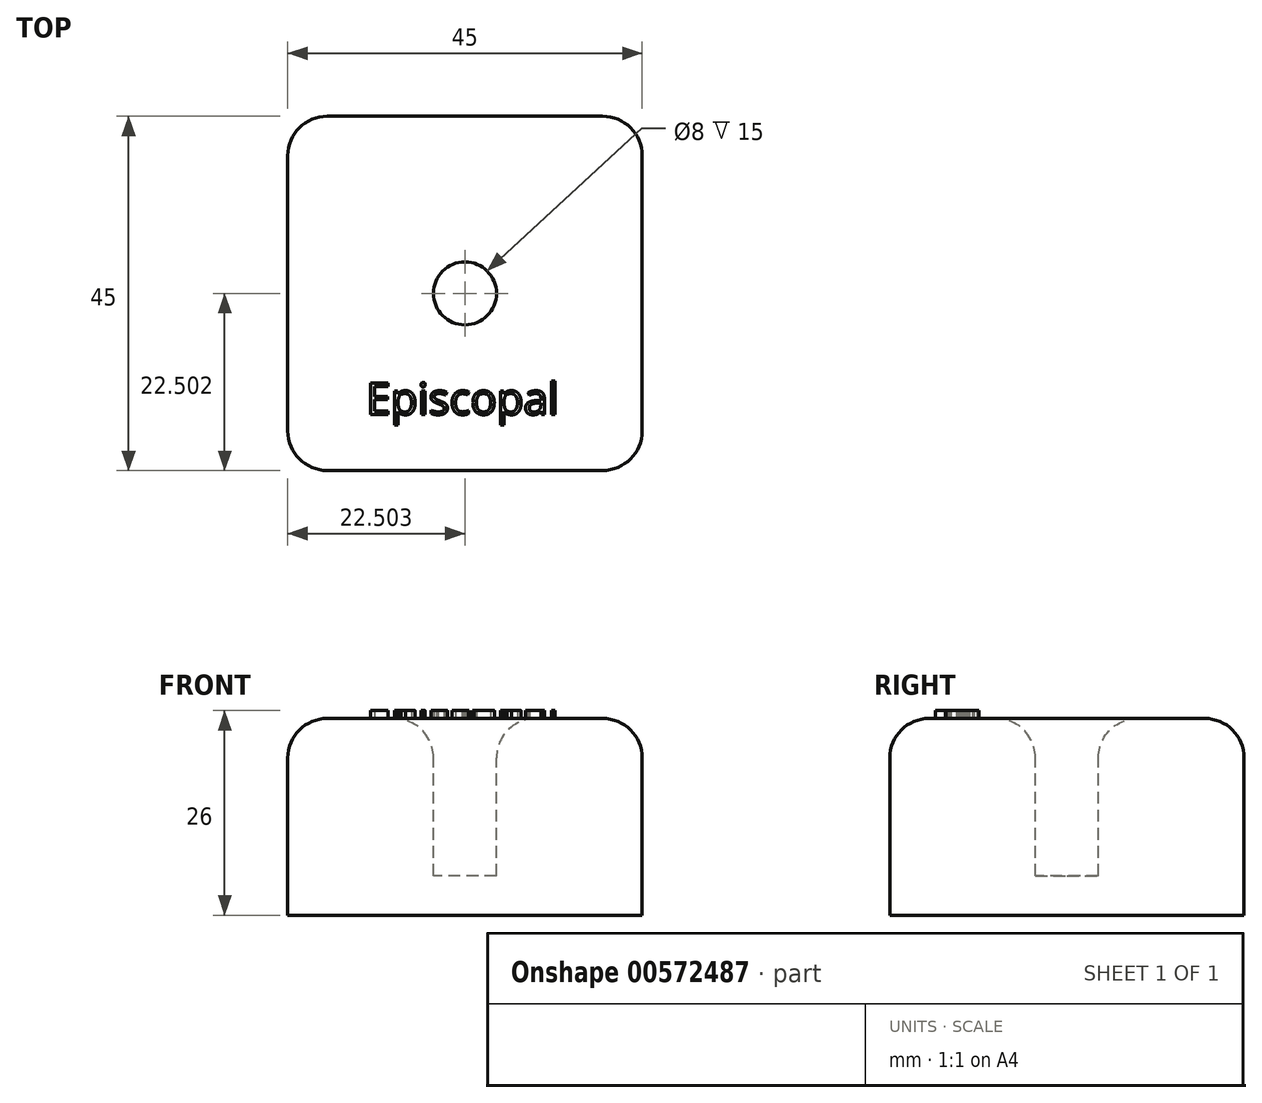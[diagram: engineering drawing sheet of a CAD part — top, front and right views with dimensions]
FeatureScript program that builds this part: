
annotation { "Feature Type Name" : "Feature", "Feature Type Description" : "" }
export const myFeature = defineFeature(function(context is Context, id is Id, definition is map)
    precondition{}
    {
        {
            var Q0;
            Q0=qCreatedBy(makeId("Top.planeOp"),FACE);
            var sketch = newSketch(context, id + "F0", { "sketchPlane" : qUnion([Q0])});
            skLineSegment(sketch, "E0.bottom", {"start": v(-22.96, 30.91) * mm, "end": v(22.04, 30.91) * mm});
            skLineSegment(sketch, "E0.top", {"start": v(-22.96, -14.09) * mm, "end": v(22.04, -14.09) * mm});
            skLineSegment(sketch, "E0.left", {"start": v(-22.96, 30.91) * mm, "end": v(-22.96, -14.09) * mm});
            skLineSegment(sketch, "E0.right", {"start": v(22.04, 30.91) * mm, "end": v(22.04, -14.09) * mm});
            skSolve(sketch);
        }
        {
            var Q0;
            Q0=makeQuery(id+"F0.imprint","IMPRINT",FACE,{"disambiguationData":[TD([[makeQuery(id+"F0.imprint","IMPRINT",EDGE,{"derivedFrom":sQuery(id+"F0.wireOp",EDGE,"E0.bottom")}),-1.0]])]});
            extrude(context, id + "F1", {"entities" : qUnion([Q0]), "depth" : 25 * mm, "offsetDistance" : 25 * mm});
        }
        {
            var Q0;
            Q0=makeQuery(id+"F1.opExtrude","CAP_FACE",FACE,{"disambiguationData":[OSD([sQuery(id+"F0.wireOp",EDGE,"E0.bottom"),sQuery(id+"F0.wireOp",EDGE,"E0.top"),sQuery(id+"F0.wireOp",EDGE,"E0.left"),sQuery(id+"F0.wireOp",EDGE,"E0.right")])],"isStart":false});
            var sketch = newSketch(context, id + "F2", { "sketchPlane" : qUnion([Q0])});
            skCircle(sketch, "E1", {"center": v(-0.46, 8.41) * mm, "radius": 4 * mm});
            skSolve(sketch);
        }
        {
            var Q0;
            Q0=makeQuery(id+"F2.imprint","IMPRINT",FACE,{"disambiguationData":[TD([[makeQuery(id+"F2.imprint","IMPRINT",EDGE,{"derivedFrom":sQuery(id+"F2.wireOp",EDGE,"E1")}),1.0]])]});
            extrude(context, id + "F3", {"entities" : qUnion([Q0]), "operationType" : NewBodyOperationType.REMOVE, "oppositeDirection" : true, "depth" : 20 * mm, "offsetDistance" : 25 * mm});
        }
        {
            var Q0;
            Q0=makeQuery(id+"F1.opExtrude","CAP_FACE",FACE,{"disambiguationData":[OSD([sQuery(id+"F0.wireOp",EDGE,"E0.bottom"),sQuery(id+"F0.wireOp",EDGE,"E0.top"),sQuery(id+"F0.wireOp",EDGE,"E0.left"),sQuery(id+"F0.wireOp",EDGE,"E0.right")])],"isStart":false});
            var Q1;
            Q1=makeQuery(id+"F1.opExtrude","SWEPT_EDGE",EDGE,{"disambiguationData":[OSD([sQuery(id+"F0.wireOp",EDGE,"E0.bottom"),sQuery(id+"F0.wireOp",EDGE,"E0.left")])]});
            var Q2;
            Q2=makeQuery(id+"F1.opExtrude","SWEPT_EDGE",EDGE,{"disambiguationData":[OSD([sQuery(id+"F0.wireOp",EDGE,"E0.bottom"),sQuery(id+"F0.wireOp",EDGE,"E0.right")])]});
            var Q3;
            Q3=makeQuery(id+"F1.opExtrude","SWEPT_EDGE",EDGE,{"disambiguationData":[OSD([sQuery(id+"F0.wireOp",EDGE,"E0.top"),sQuery(id+"F0.wireOp",EDGE,"E0.right")])]});
            var Q4;
            Q4=makeQuery(id+"F1.opExtrude","SWEPT_EDGE",EDGE,{"disambiguationData":[OSD([sQuery(id+"F0.wireOp",EDGE,"E0.top"),sQuery(id+"F0.wireOp",EDGE,"E0.left")])]});
            fillet(context, id + "F4", {"entities" : qUnion([Q0, Q1, Q2, Q3, Q4]), "radius" : 5 * mm, "tangentPropagation" : true, "allowEdgeOverflow" : false});
        }
        {
            var Q0;
            Q0=makeQuery(id+"F1.opExtrude","CAP_FACE",FACE,{"disambiguationData":[OSD([sQuery(id+"F0.wireOp",EDGE,"E0.bottom"),sQuery(id+"F0.wireOp",EDGE,"E0.top"),sQuery(id+"F0.wireOp",EDGE,"E0.left"),sQuery(id+"F0.wireOp",EDGE,"E0.right")])],"isStart":false});
            var sketch = newSketch(context, id + "F5", { "sketchPlane" : qUnion([Q0])});
            skText(sketch, "E2", { "text": "Episcopal", "fontName": "OpenSans-Regular.ttf"});
            const initialGuessF5  = {"E2": [-0.01297, -0.00697, 1, 0, 0.004]};
            skSetInitialGuess(sketch, initialGuessF5);
            skSolve(sketch);
        }
        {
            var Q0;
            Q0 = qSketchRegion(id + "F5", true);
            extrude(context, id + "F6", {"entities" : qUnion([Q0]), "operationType" : NewBodyOperationType.ADD, "depth" : 1 * mm, "offsetDistance" : 25 * mm});
        }
    });
